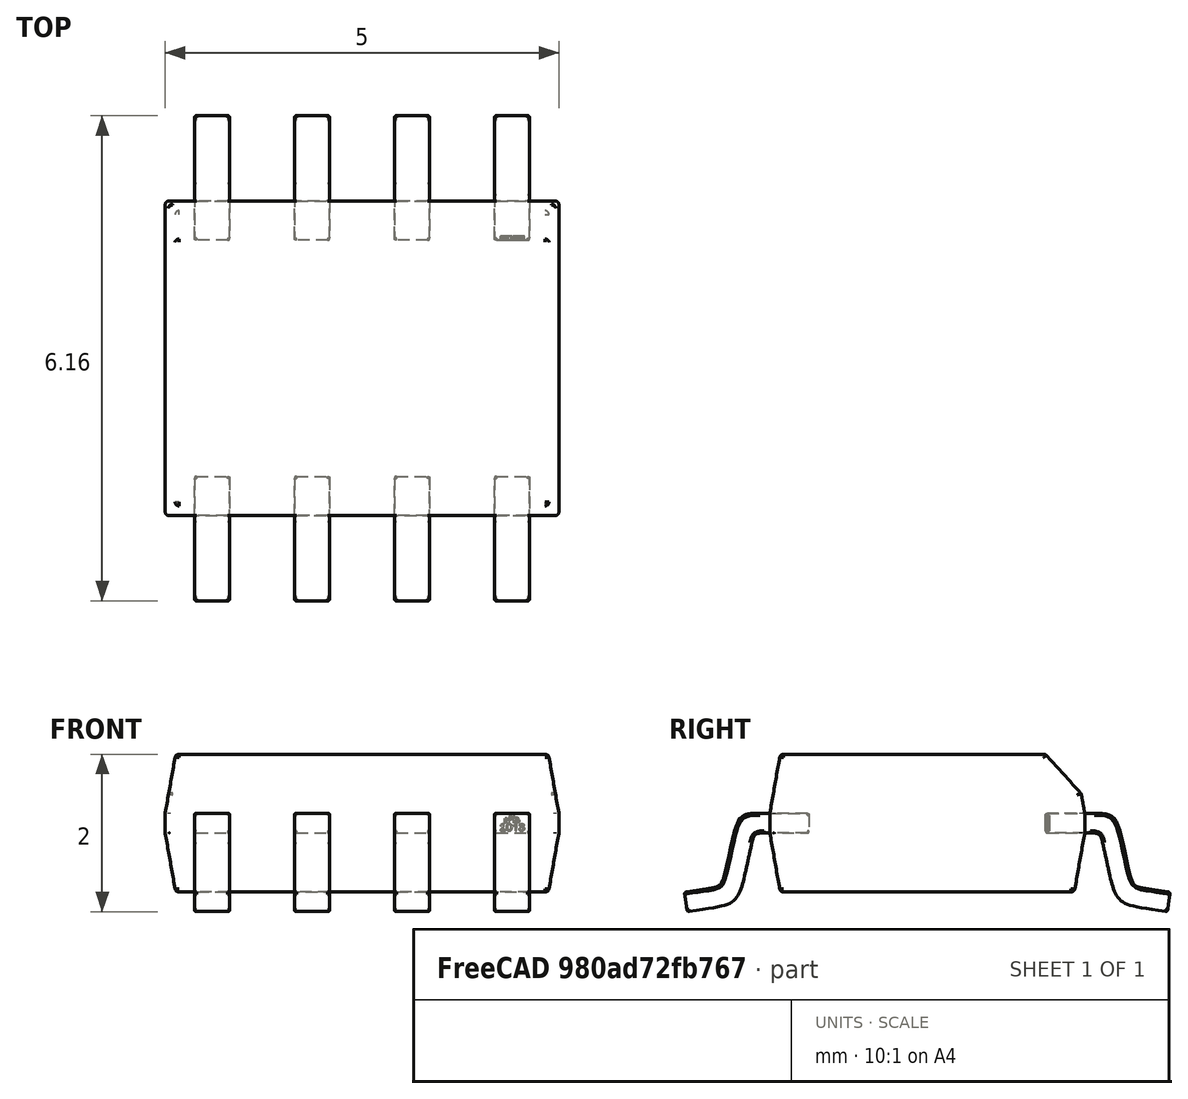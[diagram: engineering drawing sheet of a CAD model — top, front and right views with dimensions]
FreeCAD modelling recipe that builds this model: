
FCSTD DOCUMENT  (FreeCAD 0.19R24267 +99 (Git))
Label: SOIC8N
License: All rights reserved
LicenseURL: http://en.wikipedia.org/wiki/All_rights_reserved
objects: Part::Feature×9, Part::Compound×2, Part::MultiFuse×1
note: 12 computed .brp shape members not serialized (recipe doc carries the construction recipe); baked Part::Feature solids carry a one-line shape summary decoded from their .brp

FEATURE [Part::Feature] Part__Feature  label="Document.0"
  shape: bbox 7.02 x 6.02 x 3.71 mm, 64 faces (baked)
FEATURE [Part::Feature] Part__Feature001  label="Document.1"
  shape: bbox 1.45 x 2.157 x 2.25 mm, 38 faces (baked)
FEATURE [Part::Feature] Part__Feature002  label="Document.2"
  shape: bbox 1.45 x 2.157 x 2.25 mm, 38 faces (baked)
FEATURE [Part::Feature] Part__Feature003  label="Document.3"
  shape: bbox 1.45 x 2.157 x 2.25 mm, 38 faces (baked)
FEATURE [Part::Feature] Part__Feature004  label="Document.4"
  shape: bbox 1.45 x 2.157 x 2.25 mm, 38 faces (baked)
FEATURE [Part::Feature] Part__Feature005  label="Document.5"
  shape: bbox 1.45 x 2.157 x 2.256 mm, 38 faces (baked)
FEATURE [Part::Feature] Part__Feature006  label="Document.6"
  shape: bbox 1.45 x 2.157 x 2.256 mm, 38 faces (baked)
FEATURE [Part::Feature] Part__Feature007  label="Document.7"
  shape: bbox 1.45 x 2.157 x 2.256 mm, 38 faces (baked)
FEATURE [Part::Feature] Part__Feature008  label="Document.8"
  shape: bbox 1.45 x 2.157 x 2.25 mm, 72 faces (baked)
FEATURE [Part::MultiFuse] Fusion
  Shapes = -> [Part__Feature001,Part__Feature002,Part__Feature003,Part__Feature004,Part__Feature005,Part__Feature006,Part__Feature007,Part__Feature008]
FEATURE [Part::Compound] Compound
  Links = -> [Part__Feature]
FEATURE [Part::Compound] Compound001
  Links = -> [Fusion,Compound]
